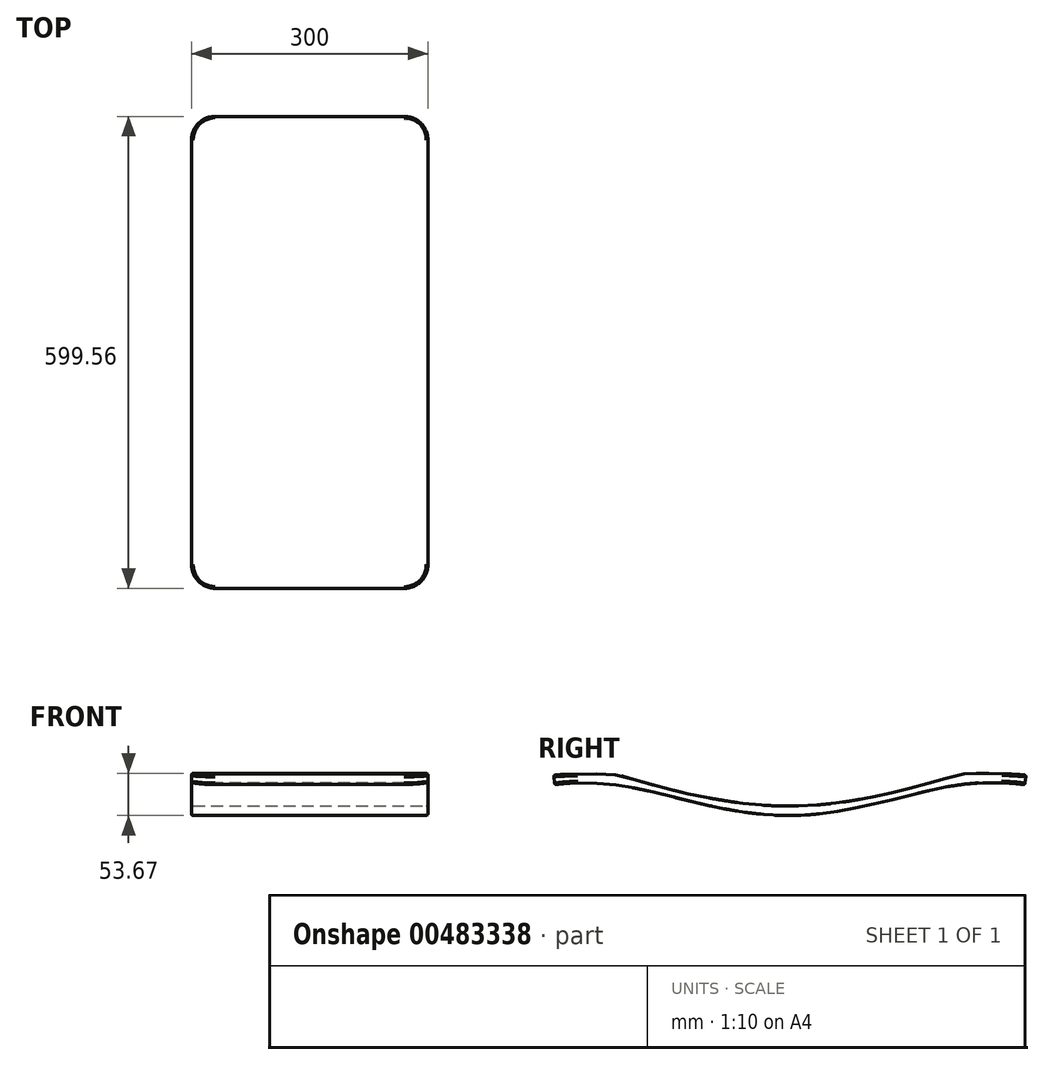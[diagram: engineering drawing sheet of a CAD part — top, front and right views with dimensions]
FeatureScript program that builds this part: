
annotation { "Feature Type Name" : "Feature", "Feature Type Description" : "" }
export const myFeature = defineFeature(function(context is Context, id is Id, definition is map)
    precondition{}
    {
        {
            var Q0;
            Q0=qCreatedBy(makeId("Right.planeOp"),FACE);
            var sketch = newSketch(context, id + "F0", { "sketchPlane" : qUnion([Q0])});
            skPoint(sketch, "E0.orphan", {"position": v(-210, 15.47) * mm});
            skPoint(sketch, "E1.start.orphan", {"position": v(0, -22.66) * mm});
            skFitSpline(sketch, "E2", {"points": [v(-300, 17.34) * mm, v(-229.51, 18.55) * mm, v(-210, 15.47) * mm, v(0, -21.83) * mm, v(210, 16.46) * mm, v(228.88, 19.5) * mm, v(248.47, 19.78) * mm, v(300, 17.34) * mm], "startDerivative": vector(302.47, 35.77) * mm, "endDerivative": vector(302.47, -35.77) * mm});
            skFitSpline(sketch, "E3.0", {"points": [v(-298.6, 5.43) * mm, v(-292.52, 6.14) * mm, v(-281.71, 7.15) * mm, v(-264.3, 7.66) * mm, v(-249.86, 7.46) * mm, v(-236.78, 6.65) * mm, v(-225.73, 5.54) * mm, v(-218.6, 4.63) * mm, v(-212.78, 3.77) * mm, v(-206.86, 2.8) * mm, v(-199.25, 1.42) * mm, v(-189.84, -0.5) * mm, v(-176.9, -3.34) * mm, v(-160.1, -7.33) * mm, v(-139.02, -12.52) * mm, v(-117.16, -17.8) * mm, v(-94.64, -22.84) * mm, v(-71.56, -27.32) * mm, v(-51.94, -30.32) * mm, v(-36.06, -32.12) * mm, v(-24.07, -33.12) * mm, v(-14.03, -33.63) * mm, v(-5.96, -33.82) * mm, v(0.1, -33.85) * mm, v(6.16, -33.76) * mm, v(14.22, -33.5) * mm, v(24.26, -32.9) * mm, v(36.24, -31.78) * mm, v(52.1, -29.85) * mm, v(71.71, -26.68) * mm, v(94.77, -22.02) * mm, v(117.27, -16.84) * mm, v(139.1, -11.46) * mm, v(160.13, -6.22) * mm, v(176.9, -2.22) * mm, v(189.8, 0.6) * mm, v(199.2, 2.48) * mm, v(206.78, 3.82) * mm, v(212.69, 4.74) * mm, v(218.5, 5.56) * mm, v(225.6, 6.4) * mm, v(236.62, 7.4) * mm, v(249.68, 8.03) * mm, v(264.12, 8.03) * mm, v(277.2, 7.46) * mm, v(288.81, 6.53) * mm, v(295.51, 5.79) * mm, v(298.6, 5.43) * mm]});
            skLineSegment(sketch, "E4", {"start": v(-300, 17.34) * mm, "end": v(-298.6, 5.43) * mm});
            skLineSegment(sketch, "E5", {"start": v(300, 17.34) * mm, "end": v(298.6, 5.43) * mm});
            skLineSegment(sketch, "E6", {"start": v(-309.05, -52.66) * mm, "end": v(312.48, -52.66) * mm});
            skSolve(sketch);
        }
        {
            var Q0;
            Q0 = qSketchRegion(id + "F0", true);
            extrude(context, id + "F1", {"entities" : qUnion([Q0]), "depth" : 300 * mm});
        }
        {
            var Q0;
            Q0=makeQuery(id+"F1.opExtrude","CAP_EDGE",EDGE,{"disambiguationData":[OSD([sQuery(id+"F0.wireOp",EDGE,"E4")])],"isStart":false});
            var Q1;
            Q1=makeQuery(id+"F1.opExtrude","CAP_EDGE",EDGE,{"disambiguationData":[OSD([sQuery(id+"F0.wireOp",EDGE,"E4")])],"isStart":true});
            var Q2;
            Q2=makeQuery(id+"F1.opExtrude","CAP_EDGE",EDGE,{"disambiguationData":[OSD([sQuery(id+"F0.wireOp",EDGE,"E5")])],"isStart":true});
            var Q3;
            Q3=makeQuery(id+"F1.opExtrude","CAP_EDGE",EDGE,{"disambiguationData":[OSD([sQuery(id+"F0.wireOp",EDGE,"E5")])],"isStart":false});
            fillet(context, id + "F2", {"entities" : qUnion([Q0, Q1, Q2, Q3]), "radius" : 30 * mm, "tangentPropagation" : true, "allowEdgeOverflow" : false});
        }
        {
            var Q0;
            Q0=makeQuery(id+"F1.opExtrude","SWEPT_FACE",FACE,{"disambiguationData":[OSD([sQuery(id+"F0.wireOp",EDGE,"E2")])]});
            var Q1;
            Q1=makeQuery(id+"F1.opExtrude","CAP_EDGE",EDGE,{"disambiguationData":[OSD([sQuery(id+"F0.wireOp",EDGE,"E3.0")])],"isStart":false});
            var Q2;
            Q2=makeQuery(id+"F2.opFillet","BLEND_EDGE",EDGE,{"blendedFrom":[makeQuery(id+"F1.opExtrude","CAP_EDGE",EDGE,{"disambiguationData":[OSD([sQuery(id+"F0.wireOp",EDGE,"E4")])],"isStart":false}),makeQuery(id+"F1.opExtrude","SWEPT_FACE",FACE,{"disambiguationData":[OSD([sQuery(id+"F0.wireOp",EDGE,"E3.0")])]})],"blendedInto":[makeQuery(id+"F1.opExtrude","SWEPT_FACE",FACE,{"disambiguationData":[OSD([sQuery(id+"F0.wireOp",EDGE,"E3.0")])]})]});
            var Q3;
            Q3=makeQuery(id+"F1.opExtrude","SWEPT_EDGE",EDGE,{"disambiguationData":[OSD([sQuery(id+"F0.wireOp",EDGE,"E3.0"),sQuery(id+"F0.wireOp",EDGE,"E4")])]});
            var Q4;
            Q4=makeQuery(id+"F2.opFillet","BLEND_EDGE",EDGE,{"blendedFrom":[makeQuery(id+"F1.opExtrude","CAP_EDGE",EDGE,{"disambiguationData":[OSD([sQuery(id+"F0.wireOp",EDGE,"E4")])],"isStart":true}),makeQuery(id+"F1.opExtrude","SWEPT_FACE",FACE,{"disambiguationData":[OSD([sQuery(id+"F0.wireOp",EDGE,"E3.0")])]})],"blendedInto":[makeQuery(id+"F1.opExtrude","SWEPT_FACE",FACE,{"disambiguationData":[OSD([sQuery(id+"F0.wireOp",EDGE,"E3.0")])]})]});
            var Q5;
            Q5=makeQuery(id+"F2.opFillet","BLEND_EDGE",EDGE,{"blendedFrom":[makeQuery(id+"F1.opExtrude","CAP_EDGE",EDGE,{"disambiguationData":[OSD([sQuery(id+"F0.wireOp",EDGE,"E5")])],"isStart":false}),makeQuery(id+"F1.opExtrude","SWEPT_FACE",FACE,{"disambiguationData":[OSD([sQuery(id+"F0.wireOp",EDGE,"E3.0")])]})],"blendedInto":[makeQuery(id+"F1.opExtrude","SWEPT_FACE",FACE,{"disambiguationData":[OSD([sQuery(id+"F0.wireOp",EDGE,"E3.0")])]})]});
            var Q6;
            Q6=makeQuery(id+"F1.opExtrude","SWEPT_EDGE",EDGE,{"disambiguationData":[OSD([sQuery(id+"F0.wireOp",EDGE,"E3.0"),sQuery(id+"F0.wireOp",EDGE,"E5")])]});
            var Q7;
            Q7=makeQuery(id+"F2.opFillet","BLEND_EDGE",EDGE,{"blendedFrom":[makeQuery(id+"F1.opExtrude","CAP_EDGE",EDGE,{"disambiguationData":[OSD([sQuery(id+"F0.wireOp",EDGE,"E5")])],"isStart":true}),makeQuery(id+"F1.opExtrude","SWEPT_FACE",FACE,{"disambiguationData":[OSD([sQuery(id+"F0.wireOp",EDGE,"E3.0")])]})],"blendedInto":[makeQuery(id+"F1.opExtrude","SWEPT_FACE",FACE,{"disambiguationData":[OSD([sQuery(id+"F0.wireOp",EDGE,"E3.0")])]})]});
            var Q8;
            Q8=makeQuery(id+"F1.opExtrude","CAP_EDGE",EDGE,{"disambiguationData":[OSD([sQuery(id+"F0.wireOp",EDGE,"E3.0")])],"isStart":true});
            fillet(context, id + "F3", {"entities" : qUnion([Q0, Q1, Q2, Q3, Q4, Q5, Q6, Q7, Q8]), "radius" : 2 * mm, "tangentPropagation" : true, "allowEdgeOverflow" : false});
        }
    });
